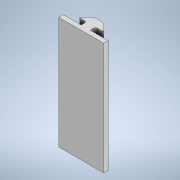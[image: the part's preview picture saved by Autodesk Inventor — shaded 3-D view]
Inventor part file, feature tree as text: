
AUTODESK INVENTOR PART (.ipt)
format: ipt  version: 2020 (Build 240168000, 168)  size: 148,992 bytes
history: native  units: mm
features: other x2, extrude x1, sketch x1
ambient origin geometry x8: Origin, YZ Plane, XZ Plane, XY Plane, X Axis, Y Axis, Z Axis, Center Point
bodies: Body1 (feature_tree)
feature tree (4):
  other  "Bryła1"
  extrude  "Wyciągnięcie proste1"  Depth=2.0mm
  other  "Pogrubienie1"
  sketch  "Szkic1"
